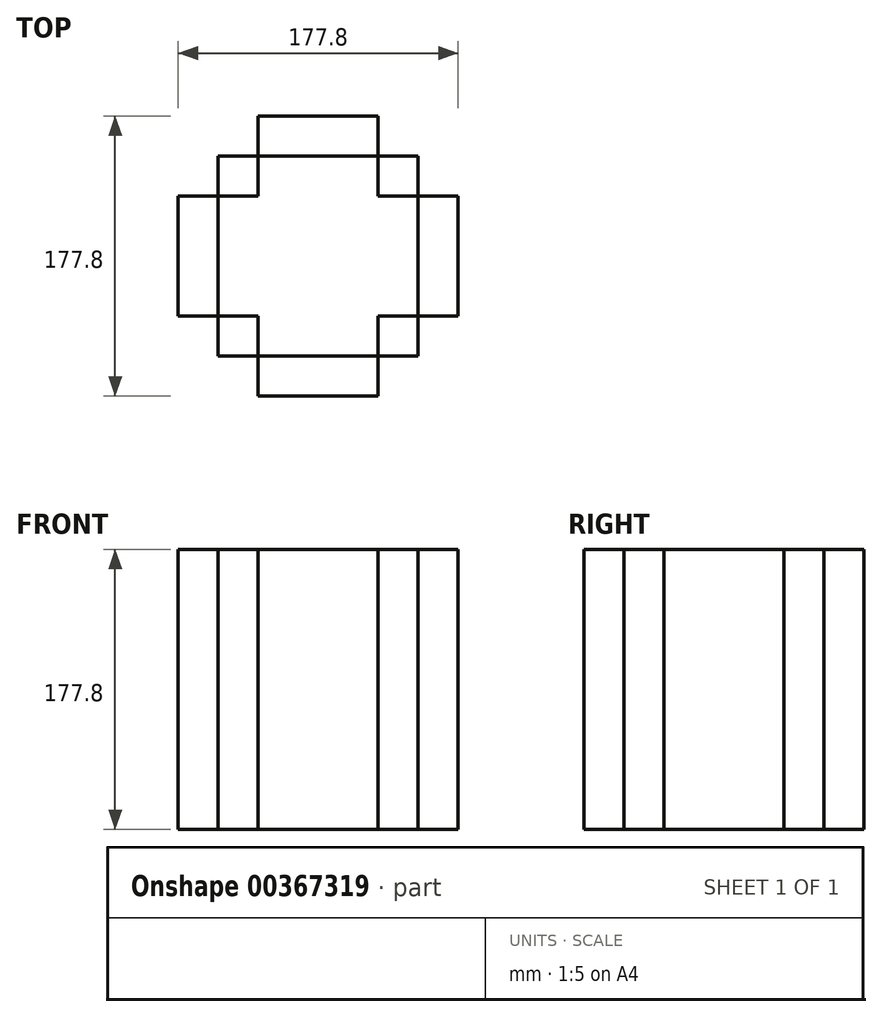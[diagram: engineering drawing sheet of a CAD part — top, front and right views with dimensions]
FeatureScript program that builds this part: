
annotation { "Feature Type Name" : "Feature", "Feature Type Description" : "" }
export const myFeature = defineFeature(function(context is Context, id is Id, definition is map)
    precondition{}
    {
        {
            var Q0;
            Q0=qCreatedBy(makeId("Top.planeOp"),FACE);
            var sketch = newSketch(context, id + "F0", { "sketchPlane" : qUnion([Q0])});
            skLineSegment(sketch, "E0.bottom", {"start": v(-88.9, 88.9) * mm, "end": v(88.9, 88.9) * mm});
            skLineSegment(sketch, "E0.top", {"start": v(-88.9, -88.9) * mm, "end": v(88.9, -88.9) * mm});
            skLineSegment(sketch, "E0.left", {"start": v(-88.9, 88.9) * mm, "end": v(-88.9, -88.9) * mm});
            skLineSegment(sketch, "E0.right", {"start": v(88.9, 88.9) * mm, "end": v(88.9, -88.9) * mm});
            skSolve(sketch);
        }
        {
            var Q0;
            Q0=makeQuery(id+"F0.imprint","IMPRINT",FACE,{"disambiguationData":[TD([[makeQuery(id+"F0.imprint","IMPRINT",EDGE,{"derivedFrom":sQuery(id+"F0.wireOp",EDGE,"E0.bottom")}),-1.0]])]});
            var sketch = newSketch(context, id + "F1", { "sketchPlane" : qUnion([Q0])});
            skLineSegment(sketch, "E1.bottom", {"start": v(-88.9, 38.1) * mm, "end": v(-63.5, 38.1) * mm});
            skLineSegment(sketch, "E1.top", {"start": v(-88.9, -38.1) * mm, "end": v(-63.5, -38.1) * mm});
            skLineSegment(sketch, "E1.left", {"start": v(-88.9, 38.1) * mm, "end": v(-88.9, -38.1) * mm});
            skLineSegment(sketch, "E1.right", {"start": v(-63.5, 38.1) * mm, "end": v(-63.5, -38.1) * mm});
            skLineSegment(sketch, "E2.bottom", {"start": v(-38.1, 88.9) * mm, "end": v(38.1, 88.9) * mm});
            skLineSegment(sketch, "E2.top", {"start": v(-38.1, 63.5) * mm, "end": v(38.1, 63.5) * mm});
            skLineSegment(sketch, "E2.left", {"start": v(-38.1, 88.9) * mm, "end": v(-38.1, 63.5) * mm});
            skLineSegment(sketch, "E2.right", {"start": v(38.1, 88.9) * mm, "end": v(38.1, 63.5) * mm});
            skLineSegment(sketch, "E3.bottom", {"start": v(63.5, 38.1) * mm, "end": v(88.9, 38.1) * mm});
            skLineSegment(sketch, "E3.top", {"start": v(63.5, -38.1) * mm, "end": v(88.9, -38.1) * mm});
            skLineSegment(sketch, "E3.left", {"start": v(63.5, 38.1) * mm, "end": v(63.5, -38.1) * mm});
            skLineSegment(sketch, "E3.right", {"start": v(88.9, 38.1) * mm, "end": v(88.9, -38.1) * mm});
            skLineSegment(sketch, "E4.bottom", {"start": v(-38.1, -63.5) * mm, "end": v(38.1, -63.5) * mm});
            skLineSegment(sketch, "E4.top", {"start": v(-38.1, -88.9) * mm, "end": v(38.1, -88.9) * mm});
            skLineSegment(sketch, "E4.left", {"start": v(-38.1, -63.5) * mm, "end": v(-38.1, -88.9) * mm});
            skLineSegment(sketch, "E4.right", {"start": v(38.1, -63.5) * mm, "end": v(38.1, -88.9) * mm});
            skLineSegment(sketch, "E5.bottom", {"start": v(38.1, -38.1) * mm, "end": v(63.5, -38.1) * mm});
            skLineSegment(sketch, "E5.top", {"start": v(38.1, -63.5) * mm, "end": v(63.5, -63.5) * mm});
            skLineSegment(sketch, "E5.left", {"start": v(38.1, -38.1) * mm, "end": v(38.1, -63.5) * mm});
            skLineSegment(sketch, "E5.right", {"start": v(63.5, -38.1) * mm, "end": v(63.5, -63.5) * mm});
            skLineSegment(sketch, "E6.bottom", {"start": v(-63.5, -38.1) * mm, "end": v(-38.1, -38.1) * mm});
            skLineSegment(sketch, "E6.top", {"start": v(-63.5, -63.5) * mm, "end": v(-38.1, -63.5) * mm});
            skLineSegment(sketch, "E6.left", {"start": v(-63.5, -38.1) * mm, "end": v(-63.5, -63.5) * mm});
            skLineSegment(sketch, "E6.right", {"start": v(-38.1, -38.1) * mm, "end": v(-38.1, -63.5) * mm});
            skLineSegment(sketch, "E7.bottom", {"start": v(-63.5, 63.5) * mm, "end": v(-38.1, 63.5) * mm});
            skLineSegment(sketch, "E7.top", {"start": v(-63.5, 38.1) * mm, "end": v(-38.1, 38.1) * mm});
            skLineSegment(sketch, "E7.left", {"start": v(-63.5, 63.5) * mm, "end": v(-63.5, 38.1) * mm});
            skLineSegment(sketch, "E7.right", {"start": v(-38.1, 63.5) * mm, "end": v(-38.1, 38.1) * mm});
            skLineSegment(sketch, "E8.bottom", {"start": v(38.1, 63.5) * mm, "end": v(63.5, 63.5) * mm});
            skLineSegment(sketch, "E8.top", {"start": v(38.1, 38.1) * mm, "end": v(63.5, 38.1) * mm});
            skLineSegment(sketch, "E8.left", {"start": v(38.1, 63.5) * mm, "end": v(38.1, 38.1) * mm});
            skLineSegment(sketch, "E8.right", {"start": v(63.5, 63.5) * mm, "end": v(63.5, 38.1) * mm});
            skSolve(sketch);
        }
        {
            var Q0;
            Q0=makeQuery(id+"F1.imprint","IMPRINT",FACE,{"disambiguationData":[TD([[makeQuery(id+"F1.imprint","IMPRINT",EDGE,{"derivedFrom":sQuery(id+"F1.wireOp",EDGE,"E6.bottom")}),-1.0]])]});
            var Q1;
            Q1=makeQuery(id+"F1.imprint","IMPRINT",FACE,{"disambiguationData":[TD([[makeQuery(id+"F1.imprint","IMPRINT",EDGE,{"derivedFrom":sQuery(id+"F1.wireOp",EDGE,"E1.bottom")}),-1.0]])]});
            var Q2;
            Q2=makeQuery(id+"F1.imprint","IMPRINT",FACE,{"disambiguationData":[TD([[makeQuery(id+"F1.imprint","IMPRINT",EDGE,{"derivedFrom":sQuery(id+"F1.wireOp",EDGE,"E7.bottom")}),-1.0]])]});
            var Q3;
            Q3=makeQuery(id+"F1.imprint","IMPRINT",FACE,{"disambiguationData":[TD([[makeQuery(id+"F1.imprint","IMPRINT",EDGE,{"derivedFrom":sQuery(id+"F1.wireOp",EDGE,"E5.bottom")}),-1.0]])]});
            var Q4;
            Q4=makeQuery(id+"F1.imprint","IMPRINT",FACE,{"disambiguationData":[TD([[makeQuery(id+"F1.imprint","IMPRINT",EDGE,{"derivedFrom":sQuery(id+"F1.wireOp",EDGE,"E4.bottom")}),-1.0]])]});
            var Q5;
            Q5=makeQuery(id+"F1.imprint","IMPRINT",FACE,{"disambiguationData":[TD([[makeQuery(id+"F1.imprint","IMPRINT",EDGE,{"derivedFrom":sQuery(id+"F1.wireOp",EDGE,"E3.bottom")}),-1.0]])]});
            var Q6;
            Q6=makeQuery(id+"F1.imprint","IMPRINT",FACE,{"disambiguationData":[TD([[makeQuery(id+"F1.imprint","IMPRINT",EDGE,{"derivedFrom":sQuery(id+"F1.wireOp",EDGE,"E2.bottom")}),-1.0]])]});
            var Q7;
            Q7=makeQuery(id+"F1.imprint","IMPRINT",FACE,{"disambiguationData":[TD([[makeQuery(id+"F1.imprint","IMPRINT",EDGE,{"derivedFrom":sQuery(id+"F1.wireOp",EDGE,"E8.bottom")}),-1.0]])]});
            extrude(context, id + "F2", {"entities" : qUnion([Q0, Q1, Q2, Q3, Q4, Q5, Q6, Q7]), "depth" : 177.8 * mm});
        }
    });
